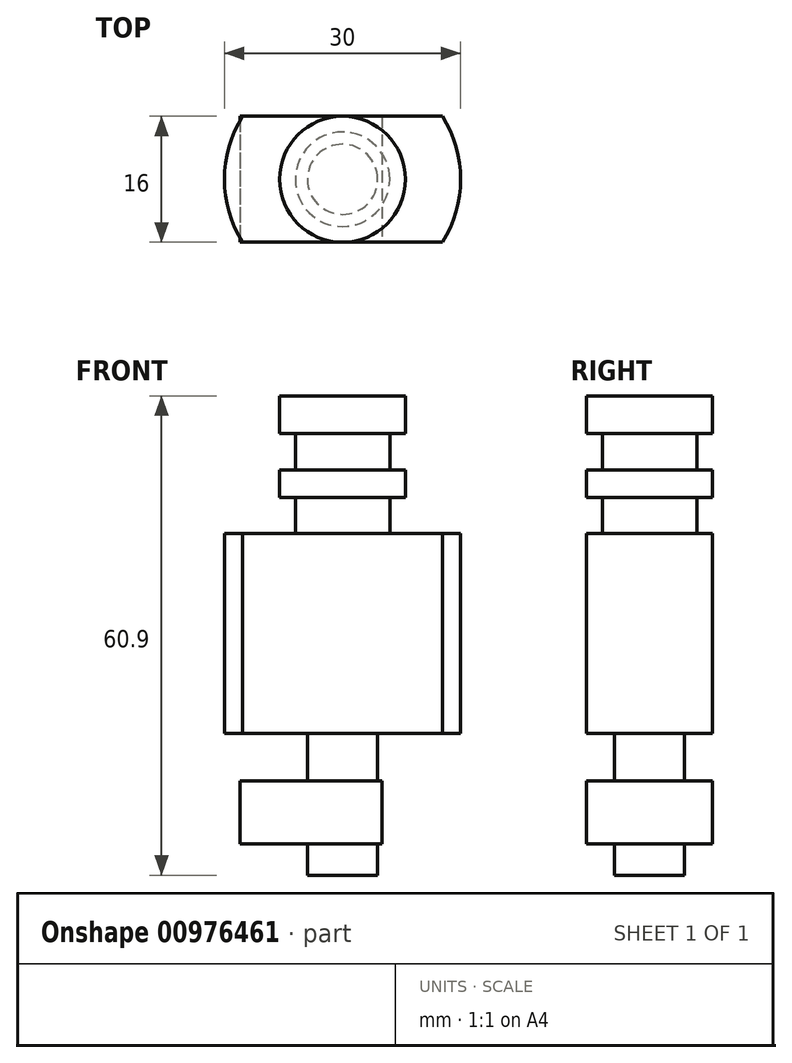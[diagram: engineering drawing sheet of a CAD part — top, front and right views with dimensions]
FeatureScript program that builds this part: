
annotation { "Feature Type Name" : "Feature", "Feature Type Description" : "" }
export const myFeature = defineFeature(function(context is Context, id is Id, definition is map)
    precondition{}
    {
        {
            var Q0;
            Q0=qCreatedBy(makeId("Top.planeOp"),FACE);
            var sketch = newSketch(context, id + "F0", { "sketchPlane" : qUnion([Q0])});
            skLineSegment(sketch, "E0.bottom", {"start": v(-13, 8) * mm, "end": v(5, 8) * mm});
            skLineSegment(sketch, "E0.top", {"start": v(-13, -8) * mm, "end": v(5, -8) * mm});
            skLineSegment(sketch, "E0.left", {"start": v(-13, 8) * mm, "end": v(-13, -8) * mm});
            skLineSegment(sketch, "E0.right", {"start": v(5, 8) * mm, "end": v(5, -8) * mm});
            skSolve(sketch);
        }
        {
            var Q0;
            Q0=qSketchRegion(id+"F0",true);
            extrude(context, id + "F1", {"entities" : qUnion([Q0]), "depth" : 8 * mm});
        }
        {
            var Q0;
            Q0=qCreatedBy(makeId("Top.planeOp"),FACE);
            var sketch = newSketch(context, id + "F2", { "sketchPlane" : qUnion([Q0])});
            skCircle(sketch, "E1", {"center": v(0, 0) * mm, "radius": 4.45 * mm});
            skSolve(sketch);
        }
        {
            var Q0;
            Q0=qSketchRegion(id+"F2",true);
            extrude(context, id + "F3", {"entities" : qUnion([Q0]), "operationType" : NewBodyOperationType.ADD, "depth" : 14 * mm, "hasSecondDirection" : true, "secondDirectionOppositeDirection" : true, "secondDirectionDepth" : 4 * mm});
        }
        {
            var Q0;
            Q0=makeQuery(id+"F3.opExtrude","CAP_FACE",FACE,{"disambiguationData":[OSD([sQuery(id+"F2.wireOp",EDGE,"E1")])],"isStart":false});
            var sketch = newSketch(context, id + "F4", { "sketchPlane" : qUnion([Q0])});
            skArc(sketch, "E2", {"start": v(-12.69, 8) * mm, "mid": v(-15, 0) * mm, "end": v(-12.69, -8) * mm});
            skLineSegment(sketch, "E3.rect.bottom", {"start": v(12.69, -8) * mm, "end": v(-12.69, -8) * mm});
            skLineSegment(sketch, "E3.rect.top", {"start": v(12.69, 8) * mm, "end": v(-12.69, 8) * mm});
            skArc(sketch, "E4.trimOffspring", {"start": v(12.69, -8) * mm, "mid": v(15, 0) * mm, "end": v(12.69, 8) * mm});
            skPoint(sketch, "E5.orphan", {"position": v(-15, -8) * mm});
            skPoint(sketch, "E6.orphan", {"position": v(-15, 8) * mm});
            skPoint(sketch, "E7.orphan", {"position": v(15, 8) * mm});
            skPoint(sketch, "E8.orphan", {"position": v(15, -8) * mm});
            skSolve(sketch);
        }
        {
            var Q0;
            Q0=qSketchRegion(id+"F4",true);
            extrude(context, id + "F5", {"entities" : qUnion([Q0]), "operationType" : NewBodyOperationType.ADD, "depth" : 25.4 * mm});
        }
        {
            var Q0;
            Q0=makeQuery(id+"F5.opExtrude","CAP_FACE",FACE,{"disambiguationData":[OSD([sQuery(id+"F4.wireOp",EDGE,"E2"),sQuery(id+"F4.wireOp",EDGE,"E3.rect.bottom"),sQuery(id+"F4.wireOp",EDGE,"E3.rect.top"),sQuery(id+"F4.wireOp",EDGE,"E4.trimOffspring")])],"isStart":false});
            var sketch = newSketch(context, id + "F6", { "sketchPlane" : qUnion([Q0])});
            skCircle(sketch, "E9", {"center": v(0, 0) * mm, "radius": 6 * mm});
            skSolve(sketch);
        }
        {
            var Q0;
            Q0=qSketchRegion(id+"F6",true);
            extrude(context, id + "F7", {"entities" : qUnion([Q0]), "operationType" : NewBodyOperationType.ADD, "depth" : 4.6 * mm});
        }
        {
            var Q0;
            Q0=makeQuery(id+"F7.opExtrude","CAP_FACE",FACE,{"disambiguationData":[OSD([sQuery(id+"F6.wireOp",EDGE,"E9")])],"isStart":false});
            var sketch = newSketch(context, id + "F8", { "sketchPlane" : qUnion([Q0])});
            skCircle(sketch, "E10", {"center": v(0, 0) * mm, "radius": 8 * mm});
            skSolve(sketch);
        }
        {
            var Q0;
            Q0=qSketchRegion(id+"F8",true);
            extrude(context, id + "F9", {"entities" : qUnion([Q0]), "operationType" : NewBodyOperationType.ADD, "depth" : 3.5 * mm});
        }
        {
            var Q0;
            Q0=makeQuery(id+"F9.opExtrude","CAP_FACE",FACE,{"disambiguationData":[OSD([sQuery(id+"F8.wireOp",EDGE,"E10")])],"isStart":false});
            var sketch = newSketch(context, id + "F10", { "sketchPlane" : qUnion([Q0])});
            skCircle(sketch, "E11", {"center": v(0, 0) * mm, "radius": 6 * mm});
            skSolve(sketch);
        }
        {
            var Q0;
            Q0=qSketchRegion(id+"F10",true);
            extrude(context, id + "F11", {"entities" : qUnion([Q0]), "operationType" : NewBodyOperationType.ADD, "depth" : 4.6 * mm});
        }
        {
            var Q0;
            Q0=makeQuery(id+"F11.opExtrude","CAP_FACE",FACE,{"disambiguationData":[OSD([sQuery(id+"F10.wireOp",EDGE,"E11")])],"isStart":false});
            var sketch = newSketch(context, id + "F12", { "sketchPlane" : qUnion([Q0])});
            skCircle(sketch, "E12", {"center": v(0, 0) * mm, "radius": 8 * mm});
            skSolve(sketch);
        }
        {
            var Q0;
            Q0=qSketchRegion(id+"F12",true);
            extrude(context, id + "F13", {"entities" : qUnion([Q0]), "operationType" : NewBodyOperationType.ADD, "depth" : 4.8 * mm});
        }
    });
